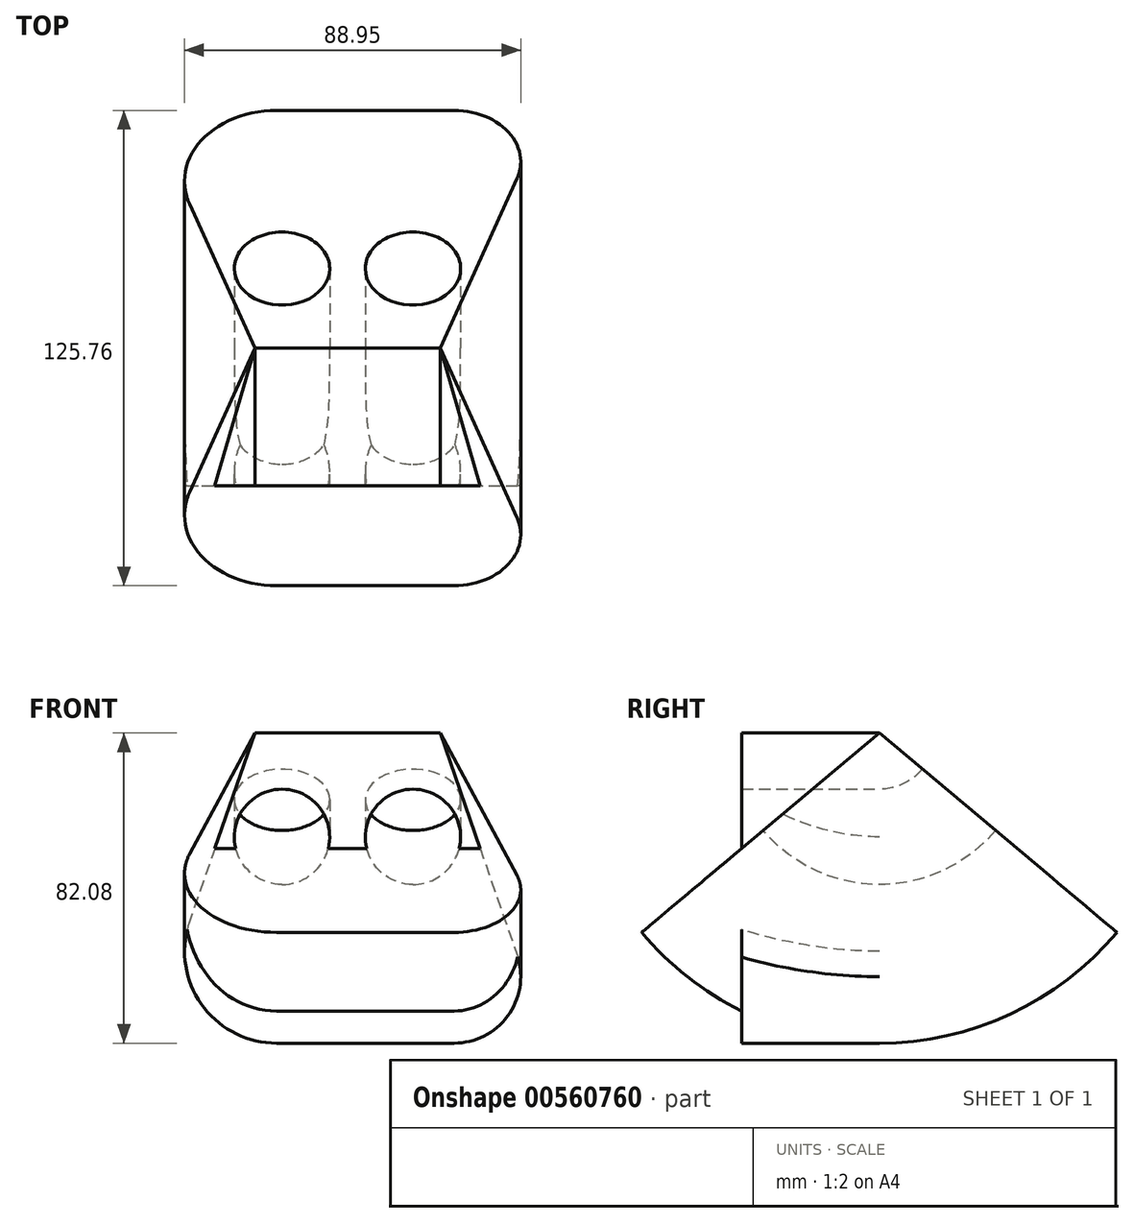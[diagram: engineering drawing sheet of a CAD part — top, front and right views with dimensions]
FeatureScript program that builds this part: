
annotation { "Feature Type Name" : "Feature", "Feature Type Description" : "" }
export const myFeature = defineFeature(function(context is Context, id is Id, definition is map)
    precondition{}
    {
        {
            var Q0;
            Q0=qCreatedBy(makeId("Front.planeOp"),FACE);
            var sketch = newSketch(context, id + "F0", { "sketchPlane" : qUnion([Q0])});
            skLineSegment(sketch, "E0.bottom", {"start": v(34.2, 0) * mm, "end": v(81.2, 0) * mm});
            skLineSegment(sketch, "E0.top", {"start": v(28.48, 82.08) * mm, "end": v(77.47, 82.08) * mm});
            skLineSegment(sketch, "E0.left", {"start": v(11.2, 32.3) * mm, "end": v(28.48, 82.08) * mm});
            skLineSegment(sketch, "E0.right", {"start": v(97.84, 23.39) * mm, "end": v(77.47, 82.08) * mm});
            skLineSegment(sketch, "E1", {"start": v(52.98, 82.08) * mm, "end": v(52.98, 0) * mm, "construction": true});
            skPoint(sketch, "E1.startSnap0", {"position": v(52.98, 0) * mm});
            skCircle(sketch, "E2", {"center": v(70.3, 54.6) * mm, "radius": 12.62 * mm});
            skCircle(sketch, "E3.MirrorC", {"center": v(35.65, 54.6) * mm, "radius": 12.62 * mm});
            skPoint(sketch, "E4.visualSharp", {"position": v(105.95, 0) * mm});
            skArc(sketch, "E4.filletArc", {"start": v(81.2, 0) * mm, "mid": v(95.55, 7.4) * mm, "end": v(97.84, 23.39) * mm});
            skPoint(sketch, "E5.visualSharp", {"position": v(0, 0) * mm});
            skArc(sketch, "E5.filletArc", {"start": v(11.2, 32.3) * mm, "mid": v(14.37, 10.22) * mm, "end": v(34.2, 0) * mm});
            skSolve(sketch);
        }
        {
            var Q0;
            Q0=makeQuery(id+"F0.imprint","IMPRINT",FACE,{"disambiguationData":[TD([[makeQuery(id+"F0.imprint","IMPRINT",EDGE,{"derivedFrom":sQuery(id+"F0.wireOp",EDGE,"E0.bottom")}),1.0]])]});
            extrude(context, id + "F1", {"entities" : qUnion([Q0]), "depth" : 36.4 * mm, "offsetDistance" : 25 * mm});
        }
        {
            var Q0;
            Q0=makeQuery(id+"F0.imprint","IMPRINT",FACE,{"disambiguationData":[TD([[makeQuery(id+"F0.imprint","IMPRINT",EDGE,{"derivedFrom":sQuery(id+"F0.wireOp",EDGE,"E0.bottom")}),1.0]])]});
            var Q1;
            Q1=sQuery(id+"F0.wireOp",EDGE,"E0.top");
            revolve(context, id + "F2", {"operationType" : NewBodyOperationType.ADD, "entities" : qUnion([Q0]), "axis" : qUnion([Q1]), "revolveType" : RevolveType.SYMMETRIC, "angle" : 100 * degree});
        }
    });
